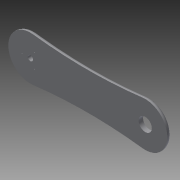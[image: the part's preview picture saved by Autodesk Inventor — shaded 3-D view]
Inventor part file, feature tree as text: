
AUTODESK INVENTOR PART (.ipt)
format: ipt  version: 2015 (Build 190159000, 159)  size: 329,728 bytes
history: native  units: mm
features: sketch x21, extrude x20, fillet x1
ambient origin geometry x8: Origin, YZ Plane, XZ Plane, XY Plane, X Axis, Y Axis, Z Axis, Center Point
bodies: Solid1 (feature_tree)
feature tree (42):
  extrude  "Extrusion1"  Depth=50.0mm
  extrude  "Extrusion2"  Depth=5.0mm
  extrude  "Extrusion3"  Depth=5.0mm TaperAngle=0.0deg
  extrude  "Extrusion4"  Depth=20.0mm
  extrude  "Extrusion5"  Depth=20.0mm
  extrude  "Extrusion6"  Depth=3.0mm
  sketch  "Sketch7"  dims[d22=3.0mm d23=5.0mm d24=0.0mm]
  extrude  "Extrusion7"  Depth=5.0mm TaperAngle=0.0deg
  extrude  "Extrusion8"  Depth=5.0mm
  extrude  "Extrusion9"  Depth=1.0mm
  extrude  "Extrusion10"  Depth=5.0mm
  extrude  "Extrusion11"  Depth=5.0mm TaperAngle=0.0deg
  sketch  "Sketch12"  dims[d44=1.0mm d45=1.0mm]
  sketch  "Sketch13"  dims[d46=1.0mm d47=5.0mm d48=0.0mm]
  extrude  "Extrusion12"  Depth=1.0mm
  extrude  "Extrusion13"  Depth=5.0mm TaperAngle=0.0deg
  extrude  "Extrusion14"  Depth=5.0mm TaperAngle=0.0deg
  extrude  "Extrusion15"  Depth=5.0mm TaperAngle=0.0deg
  extrude  "Extrusion16"  Depth=43.308mm
  extrude  "Extrusion18"  Depth=20.0mm
  extrude  "Extrusion19"  Depth=5.0mm
  extrude  "Extrusion20"  Depth=55.0mm
  extrude  "Extrusion21"  Depth=5.0mm
  fillet  "Fillet1"  Radius=5.0mm
  sketch  "Sketch1"  dims[d0=150.0mm d1=50.0mm]
  sketch  "Sketch2"  dims[d2=5.0mm d3=0.0mm d4=6.0mm]
  sketch  "Sketch3"  dims[d5=6.0mm d6=5.0mm d7=0.0mm]
  sketch  "Sketch4"  dims[d11=55.0mm d12=20.0mm]
  sketch  "Sketch5"  dims[d13=40.2mm d14=20.0mm]
  sketch  "Sketch6"  dims[d20=3.0mm d21=3.0mm]
  sketch  "Sketch8"  dims[d32=5.0mm d33=0.0mm d34=1.0mm]
  sketch  "Sketch9"  dims[d35=1.0mm d36=1.0mm]
  sketch  "Sketch10"  dims[d37=5.0mm d38=0.0mm d39=15.0mm]
  sketch  "Sketch11"  dims[d40=15.0mm d41=5.0mm d42=0.0mm]
  sketch  "Sketch14"  dims[d49=5.0mm d50=0.0mm d51=5.0mm d52=0.0mm]
  sketch  "Sketch15"  dims[d53=130.0mm d54=5.0mm d55=0.0mm]
  sketch  "Sketch16"  dims[d56=15.0mm d57=43.308mm]
  sketch  "Sketch17"  dims[d58=40.2mm d59=20.0mm]
  sketch  "Sketch19"  dims[d60=5.0mm d61=0.0mm d62=33.15mm]
  sketch  "Sketch20"  dims[d63=18.1mm d64=55.0mm]
  sketch  "Sketch21"  dims[d65=40.2mm d66=20.0mm d67=5.0mm d68=0.0mm]
  sketch  "Sketch22"  dims[d69=33.15mm d70=18.1mm d71=55.0mm d72=40.2mm d73=20.0mm d74=5.0mm d75=0.0mm d76=5.0mm d77=0.0mm d84=5.0mm d85=0.0mm d86=5.0mm d87=0.0mm d98=6.0mm d99=5.0mm d100=0.0mm d101=19.075mm d102=2.0mm d103=60.0deg d104=60.0deg d105=2.0mm d106=2.0mm d107=5.0mm d108=0.0mm d109=1.0mm d110=1.0mm d111=1.0mm d112=5.0mm d113=0.0mm d114=5.0mm d115=0.0mm d116=4.0mm]
